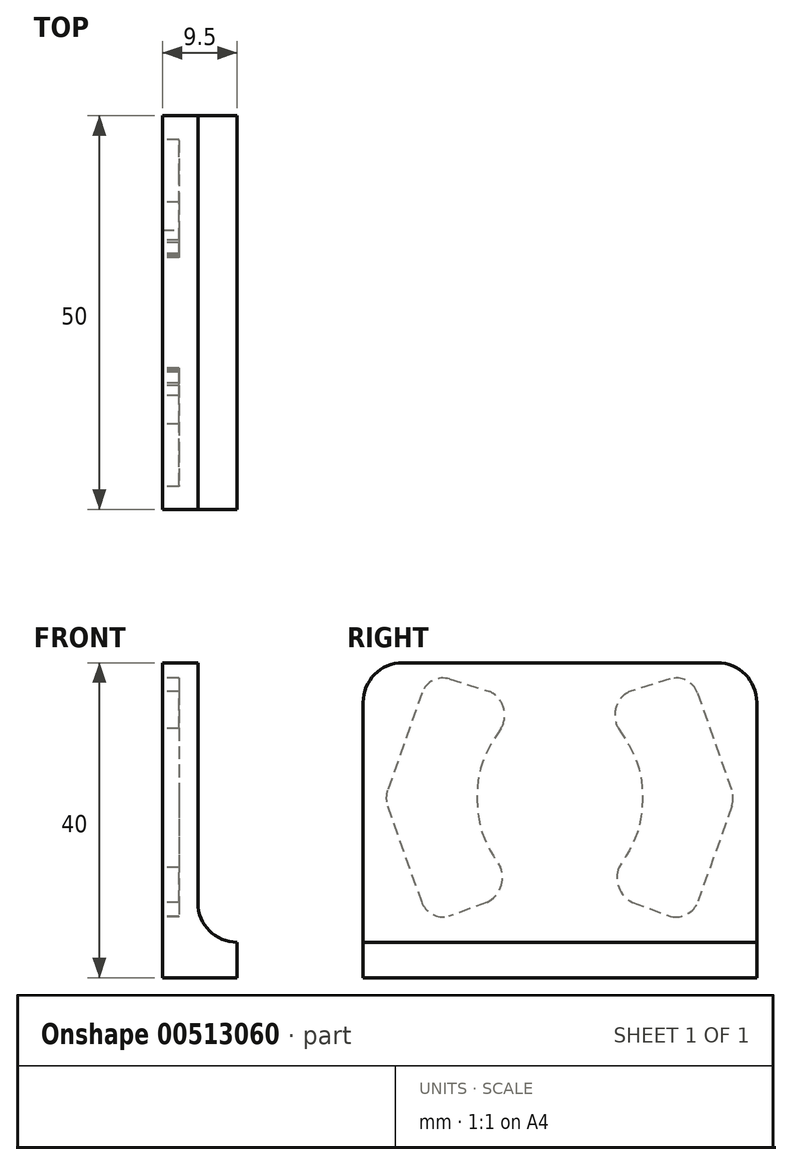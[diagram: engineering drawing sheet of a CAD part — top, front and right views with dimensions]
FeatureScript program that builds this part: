
annotation { "Feature Type Name" : "Feature", "Feature Type Description" : "" }
export const myFeature = defineFeature(function(context is Context, id is Id, definition is map)
    precondition{}
    {
        {
            var Q0;
            Q0=qCreatedBy(makeId("Front.planeOp"),FACE);
            var sketch = newSketch(context, id + "F0", { "sketchPlane" : qUnion([Q0])});
            skLineSegment(sketch, "E0", {"start": v(-15.27, 0) * mm, "end": v(-24.77, 0) * mm});
            skLineSegment(sketch, "E1", {"start": v(-24.77, 0) * mm, "end": v(-24.77, 40) * mm});
            skLineSegment(sketch, "E2", {"start": v(-24.77, 40) * mm, "end": v(-20.27, 40) * mm});
            skLineSegment(sketch, "E3", {"start": v(-20.27, 40) * mm, "end": v(-20.27, 9.5) * mm});
            skPoint(sketch, "E4.visualSharp", {"position": v(-20.27, 4.5) * mm});
            skArc(sketch, "E4.filletArc", {"start": v(-20.27, 9.5) * mm, "mid": v(-18.8, 5.96) * mm, "end": v(-15.27, 4.5) * mm});
            skLineSegment(sketch, "E5", {"start": v(-15.27, 4.5) * mm, "end": v(-15.27, 0) * mm});
            skPoint(sketch, "E6.orphan", {"position": v(35.23, 0) * mm});
            skSolve(sketch);
        }
        {
            var Q0;
            Q0=qSketchRegion(id+"F0",true);
            extrude(context, id + "F1", {"entities" : qUnion([Q0]), "depth" : 50 * mm});
        }
        {
            var Q0;
            Q0=makeQuery(id+"F1.opExtrude","CAP_EDGE",EDGE,{"disambiguationData":[OSD([sQuery(id+"F0.wireOp",EDGE,"E2")])],"isStart":false});
            fillet(context, id + "F2", {"entities" : qUnion([Q0]), "radius" : 5 * mm, "tangentPropagation" : true, "allowEdgeOverflow" : false});
        }
        {
            var Q0;
            Q0=makeQuery(id+"F1.opExtrude","CAP_EDGE",EDGE,{"disambiguationData":[OSD([sQuery(id+"F0.wireOp",EDGE,"E2")])],"isStart":true});
            fillet(context, id + "F3", {"entities" : qUnion([Q0]), "radius" : 5 * mm, "tangentPropagation" : true, "allowEdgeOverflow" : false});
        }
        {
            var Q0;
            Q0=makeQuery(id+"F1.opExtrude","SWEPT_FACE",FACE,{"disambiguationData":[OSD([sQuery(id+"F0.wireOp",EDGE,"E1")])]});
            var sketch = newSketch(context, id + "F4", { "sketchPlane" : qUnion([Q0])});
            skLineSegment(sketch, "E7", {"start": v(42.52, 36.18) * mm, "end": v(46.9, 23.81) * mm});
            skLineSegment(sketch, "E8", {"start": v(46.9, 21.8) * mm, "end": v(42.62, 9.72) * mm});
            skLineSegment(sketch, "E9", {"start": v(39, 37.93) * mm, "end": v(33.94, 36.36) * mm});
            skLineSegment(sketch, "E10", {"start": v(27.86, 29.27) * mm, "end": v(27.87, 29.1) * mm});
            skPoint(sketch, "E11.visualSharp", {"position": v(42.48, 24.1) * mm});
            skArc(sketch, "E11.filletArc", {"start": v(39.13, 7.8) * mm, "mid": v(41.24, 8.1) * mm, "end": v(42.62, 9.72) * mm});
            skArc(sketch, "E12.filletArc", {"start": v(46.9, 21.8) * mm, "mid": v(47.07, 22.8) * mm, "end": v(46.9, 23.81) * mm});
            skPoint(sketch, "E13.visualSharp", {"position": v(41.6, 38.74) * mm});
            skArc(sketch, "E13.filletArc", {"start": v(42.52, 36.18) * mm, "mid": v(41.12, 37.76) * mm, "end": v(39, 37.93) * mm});
            skArc(sketch, "E14", {"start": v(33.94, 36.36) * mm, "mid": v(32.17, 34.34) * mm, "end": v(32.5, 31.68) * mm});
            skArc(sketch, "E15", {"start": v(32.56, 14.03) * mm, "mid": v(32.53, 11.46) * mm, "end": v(34.28, 9.57) * mm});
            skLineSegment(sketch, "E16.trimOffspring", {"start": v(34.28, 9.57) * mm, "end": v(39.13, 7.8) * mm});
            skFitSpline(sketch, "E17", {"points": [v(32.5, 31.68) * mm, v(34.78, 27.56) * mm, v(35.53, 23.1) * mm, v(34.87, 18.36) * mm, v(32.56, 14.03) * mm], "startDerivative": vector(10.52, -16.1) * mm, "endDerivative": vector(-10.51, -16.47) * mm});
            skArc(sketch, "E18.MirrorCS", {"start": v(3.17, 21.8) * mm, "mid": v(3, 22.8) * mm, "end": v(3.17, 23.81) * mm});
            skLineSegment(sketch, "E19.MirrorCS", {"start": v(18.75, 29.27) * mm, "end": v(18.75, 29.1) * mm});
            skArc(sketch, "E20.MirrorCS", {"start": v(7.55, 36.18) * mm, "mid": v(8.95, 37.76) * mm, "end": v(11.06, 37.93) * mm});
            skLineSegment(sketch, "E21.MirrorCS", {"start": v(3.17, 21.8) * mm, "end": v(7.45, 9.72) * mm});
            skLineSegment(sketch, "E22.MirrorCS", {"start": v(7.55, 36.18) * mm, "end": v(3.17, 23.81) * mm});
            skPoint(sketch, "E23.MirrorP", {"position": v(8.46, 38.74) * mm});
            skPoint(sketch, "E24.MirrorP", {"position": v(7.6, 24.1) * mm});
            skArc(sketch, "E25.MirrorCS", {"start": v(16.13, 36.36) * mm, "mid": v(17.9, 34.34) * mm, "end": v(17.57, 31.68) * mm});
            skLineSegment(sketch, "E26.MirrorCS", {"start": v(11.06, 37.93) * mm, "end": v(16.13, 36.36) * mm});
            skLineSegment(sketch, "E27.MirrorCS", {"start": v(15.79, 9.57) * mm, "end": v(10.93, 7.8) * mm});
            skArc(sketch, "E28.MirrorCS", {"start": v(10.93, 7.8) * mm, "mid": v(8.83, 8.1) * mm, "end": v(7.45, 9.72) * mm});
            skFitSpline(sketch, "E29.MirrorCS", {"points": [v(17.57, 31.68) * mm, v(15.29, 27.56) * mm, v(14.53, 23.1) * mm, v(15.2, 18.36) * mm, v(17.51, 14.03) * mm], "startDerivative": vector(-10.52, -16.1) * mm, "endDerivative": vector(10.51, -16.47) * mm});
            skArc(sketch, "E30.MirrorCS", {"start": v(17.51, 14.03) * mm, "mid": v(17.53, 11.46) * mm, "end": v(15.79, 9.57) * mm});
            skSolve(sketch);
        }
        {
            var Q0;
            Q0=qSketchRegion(id+"F4",true);
            extrude(context, id + "F5", {"entities" : qUnion([Q0]), "operationType" : NewBodyOperationType.REMOVE, "oppositeDirection" : true, "depth" : 2.1 * mm});
        }
    });
